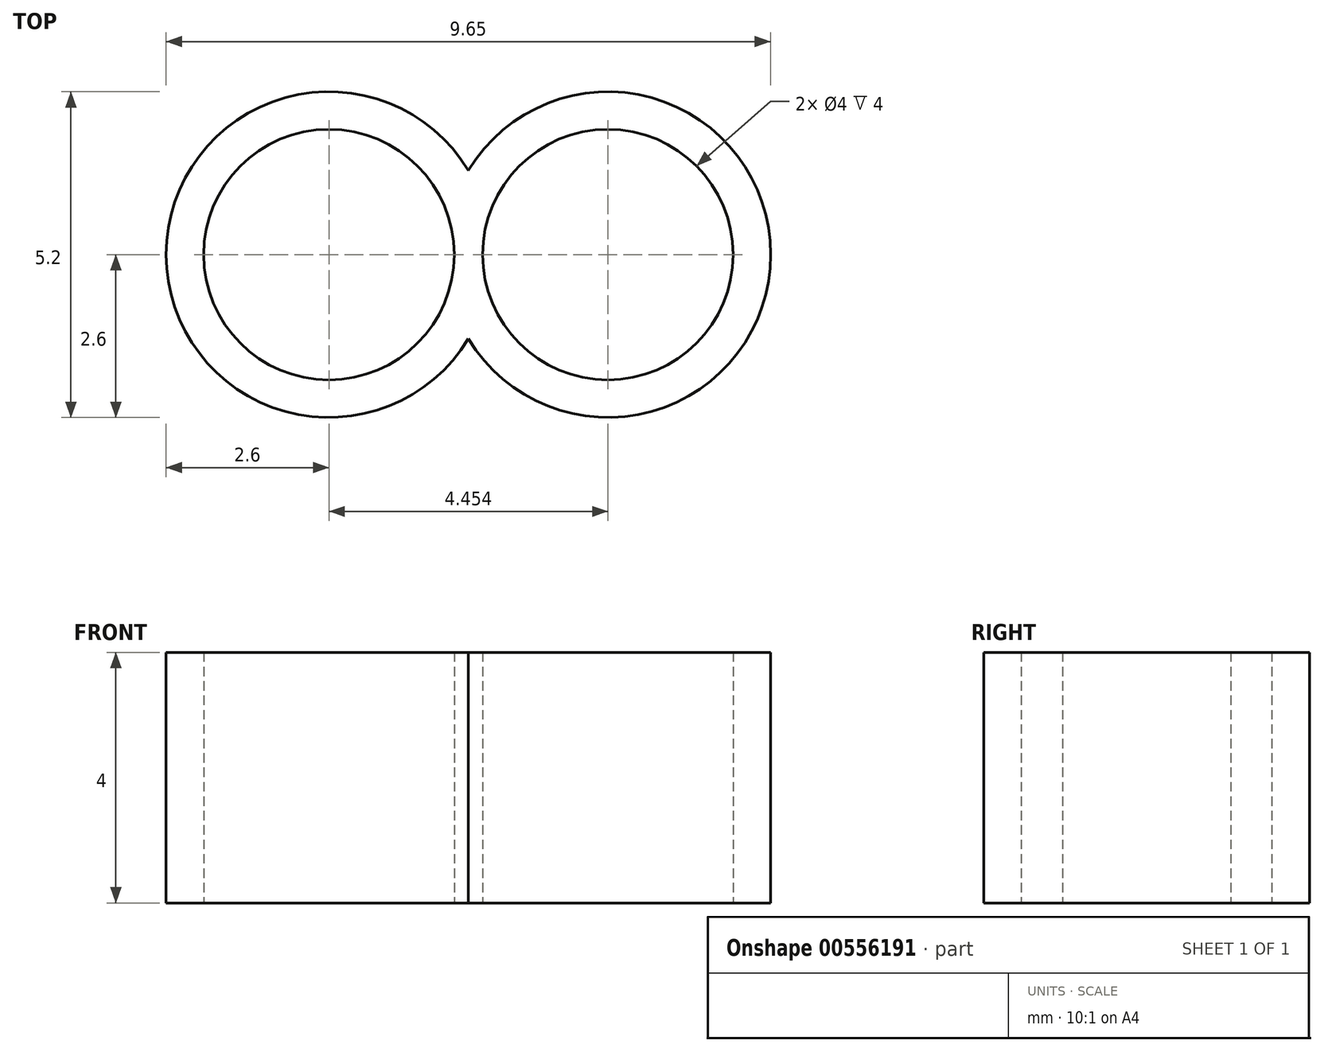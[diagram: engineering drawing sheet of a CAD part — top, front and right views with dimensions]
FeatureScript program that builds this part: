
annotation { "Feature Type Name" : "Feature", "Feature Type Description" : "" }
export const myFeature = defineFeature(function(context is Context, id is Id, definition is map)
    precondition{}
    {
        {
            var Q0;
            Q0=qCreatedBy(makeId("Top.planeOp"),FACE);
            var sketch = newSketch(context, id + "F0", { "sketchPlane" : qUnion([Q0])});
            skCircle(sketch, "E0", {"center": v(0, 0) * mm, "radius": 2 * mm});
            skArc(sketch, "E1", {"start": v(2.23, 1.34) * mm, "mid": v(-2.6, 0) * mm, "end": v(2.23, -1.34) * mm});
            skCircle(sketch, "E2", {"center": v(4.45, 0) * mm, "radius": 2 * mm});
            skArc(sketch, "E3", {"start": v(2.23, -1.34) * mm, "mid": v(7.05, 0) * mm, "end": v(2.23, 1.34) * mm});
            skSolve(sketch);
        }
        {
            var Q0;
            Q0=makeQuery(id+"F0.imprint","IMPRINT",FACE,{"disambiguationData":[TD([[makeQuery(id+"F0.imprint","IMPRINT",EDGE,{"derivedFrom":sQuery(id+"F0.wireOp",EDGE,"E0")}),-1.0]])]});
            extrude(context, id + "F1", {"entities" : qUnion([Q0]), "depth" : 4 * mm, "offsetDistance" : 25 * mm});
        }
    });
